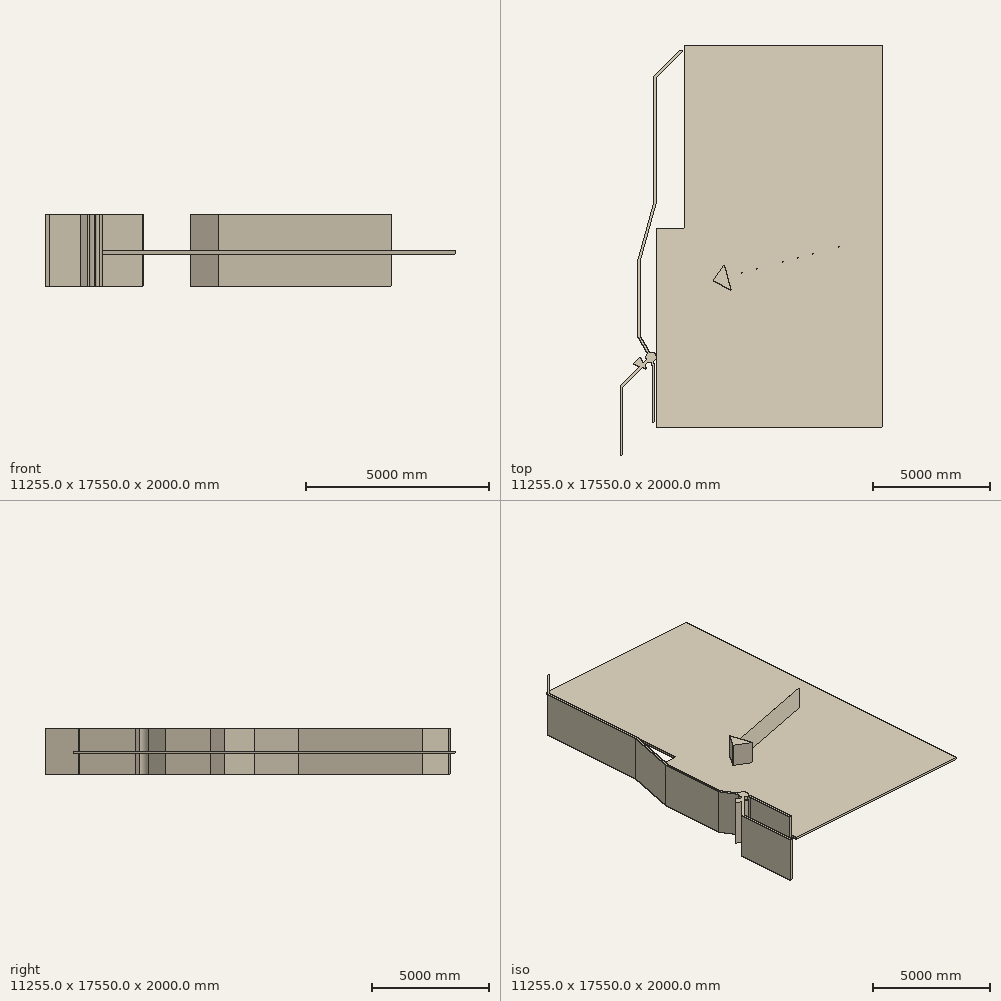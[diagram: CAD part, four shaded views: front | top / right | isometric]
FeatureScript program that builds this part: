
annotation { "Feature Type Name" : "Feature", "Feature Type Description" : "" }
export const myFeature = defineFeature(function(context is Context, id is Id, definition is map)
    precondition{}
    {
        {
            var Q0;
            Q0=qCreatedBy(makeId("Top.planeOp"),FACE);
            var sketch = newSketch(context, id + "F0", { "sketchPlane" : qUnion([Q0])});
            skLineSegment(sketch, "E0", {"start": v(-843.99, -7586.2) * mm, "end": v(-843.99, 913.8) * mm});
            skLineSegment(sketch, "E1", {"start": v(-843.99, 913.8) * mm, "end": v(356.01, 913.8) * mm});
            skLineSegment(sketch, "E2", {"start": v(356.01, 913.8) * mm, "end": v(356.01, 8763.8) * mm});
            skLineSegment(sketch, "E3", {"start": v(-843.99, -7586.2) * mm, "end": v(8856.01, -7586.2) * mm});
            skLineSegment(sketch, "E4", {"start": v(356.01, 8763.8) * mm, "end": v(8856.01, 8763.8) * mm});
            skLineSegment(sketch, "E5", {"start": v(8856.01, 8763.8) * mm, "end": v(8856.01, -7586.2) * mm});
            skSolve(sketch);
        }
        {
            var Q0;
            Q0 = qSketchRegion(id + "F0", true);
            var Q1;
            Q1 = qSketchRegion(id + "F2", true);
            extrude(context, id + "F1", {"entities" : qUnion([Q0, Q1]), "oppositeDirection" : true, "depth" : 100 * mm, "offsetDistance" : 25 * mm});
        }
        {
            var Q0;
            Q0=qCreatedBy(makeId("Top.planeOp"),FACE);
            var sketch = newSketch(context, id + "F2", { "sketchPlane" : qUnion([Q0])});
            skLineSegment(sketch, "E6", {"start": v(231.01, 10518.75) * mm, "end": v(231.01, 5123.53) * mm, "construction": true});
            skLineSegment(sketch, "E7", {"start": v(-3450.5, 8513.8) * mm, "end": v(2709.72, 8513.8) * mm, "construction": true});
            skCircle(sketch, "E8", {"center": v(231.01, 8513.8) * mm, "radius": 55 * mm});
            skLineSegment(sketch, "E9", {"start": v(-893.99, 8769.03) * mm, "end": v(-893.99, 6313.48) * mm, "construction": true});
            skLineSegment(sketch, "E10.bottom", {"start": v(192.12, 8552.7) * mm, "end": v(269.9, 8474.91) * mm});
            skLineSegment(sketch, "E10.left", {"start": v(192.12, 8552.7) * mm, "end": v(-948.99, 7411.58) * mm});
            skLineSegment(sketch, "E10.right", {"start": v(269.9, 8474.91) * mm, "end": v(-838.99, 7366.02) * mm});
            skLineSegment(sketch, "E11.left", {"start": v(-948.99, 7411.58) * mm, "end": v(-948.99, 2043.63) * mm});
            skLineSegment(sketch, "E11.right", {"start": v(-838.99, 7366.02) * mm, "end": v(-838.99, 2028.66) * mm});
            skPoint(sketch, "E12", {"position": v(-838.99, 7366.02) * mm});
            skLineSegment(sketch, "E13.left", {"start": v(-948.99, 2043.63) * mm, "end": v(-1648.99, -480.68) * mm});
            skLineSegment(sketch, "E13.right", {"start": v(-838.99, 2028.66) * mm, "end": v(-1538.99, -495.65) * mm});
            skCircle(sketch, "E14", {"center": v(-1068.99, -4586.2) * mm, "radius": 225 * mm});
            skLineSegment(sketch, "E15.left", {"start": v(-1648.99, -3691.6) * mm, "end": v(-1225.7, -4424.75) * mm});
            skLineSegment(sketch, "E15.right", {"start": v(-1538.99, -3662.13) * mm, "end": v(-1130.44, -4369.75) * mm});
            skLineSegment(sketch, "E16.left", {"start": v(-1184.37, -4779.36) * mm, "end": v(-2288.99, -5883.98) * mm});
            skLineSegment(sketch, "E16.right", {"start": v(-1262.15, -4701.58) * mm, "end": v(-2398.99, -5838.42) * mm});
            skLineSegment(sketch, "E17.left", {"start": v(-1648.99, -480.68) * mm, "end": v(-1648.99, -3691.6) * mm});
            skLineSegment(sketch, "E17.right", {"start": v(-1538.99, -495.65) * mm, "end": v(-1538.99, -3662.13) * mm});
            skPoint(sketch, "E18", {"position": v(-1538.99, -495.65) * mm});
            skPoint(sketch, "E19", {"position": v(-1648.99, -480.68) * mm});
            skPoint(sketch, "E20", {"position": v(-1262.15, -4701.58) * mm});
            skPoint(sketch, "E21", {"position": v(-1184.37, -4779.36) * mm});
            skLineSegment(sketch, "E22.top", {"start": v(-2398.99, -8786.2) * mm, "end": v(-2288.99, -8786.2) * mm});
            skLineSegment(sketch, "E22.left", {"start": v(-2398.99, -5838.42) * mm, "end": v(-2398.99, -8786.2) * mm});
            skLineSegment(sketch, "E22.right", {"start": v(-2288.99, -5883.98) * mm, "end": v(-2288.99, -8786.2) * mm});
            skPoint(sketch, "E23", {"position": v(-2288.99, -5883.98) * mm});
            skPoint(sketch, "E24", {"position": v(-2398.99, -5838.42) * mm});
            skLineSegment(sketch, "E25.bottom", {"start": v(7111.36, 175.71) * mm, "end": v(1591.41, -1303.35) * mm});
            skLineSegment(sketch, "E25.top", {"start": v(7111.87, 173.78) * mm, "end": v(1591.93, -1305.29) * mm});
            skLineSegment(sketch, "E25.left", {"start": v(7111.36, 175.71) * mm, "end": v(7111.87, 173.78) * mm});
            skLineSegment(sketch, "E25.right", {"start": v(1591.41, -1303.35) * mm, "end": v(1591.93, -1305.29) * mm});
            skLineSegment(sketch, "E26", {"start": v(1591.41, -1303.35) * mm, "end": v(2066.27, -623) * mm});
            skLineSegment(sketch, "E27", {"start": v(2066.27, -623) * mm, "end": v(2362.44, -1728.32) * mm});
            skLineSegment(sketch, "E28", {"start": v(2362.44, -1728.32) * mm, "end": v(1591.93, -1305.29) * mm});
            skLineSegment(sketch, "E29", {"start": v(-1527.33, -4581.31) * mm, "end": v(-1241.6, -5102.35) * mm});
            skLineSegment(sketch, "E30", {"start": v(-1241.6, -5102.35) * mm, "end": v(-1829.87, -4883.85) * mm});
            skLineSegment(sketch, "E31", {"start": v(-1829.87, -4883.85) * mm, "end": v(-1527.33, -4581.31) * mm});
            skCircle(sketch, "E32", {"center": v(-968.99, -7336.2) * mm, "radius": 55 * mm});
            skLineSegment(sketch, "E33.left", {"start": v(-959.4, -4782.7) * mm, "end": v(-913.99, -4952.16) * mm});
            skLineSegment(sketch, "E33.right", {"start": v(-1065.64, -4811.17) * mm, "end": v(-1023.99, -4966.64) * mm});
            skPoint(sketch, "E34", {"position": v(-913.99, -4952.16) * mm});
            skPoint(sketch, "E35", {"position": v(-1023.99, -4966.64) * mm});
            skLineSegment(sketch, "E36.trimOffspring", {"start": v(-913.99, -4952.16) * mm, "end": v(-913.99, -7336.2) * mm});
            skLineSegment(sketch, "E37.trimOffspring", {"start": v(-1023.99, -4966.64) * mm, "end": v(-1023.99, -7336.2) * mm});
            skSolve(sketch);
        }
        {
            var Q0;
            Q0 = qSketchRegion(id + "F2", true);
            extrude(context, id + "F3", {"entities" : qUnion([Q0]), "oppositeDirection" : true, "depth" : 1000 * mm, "offsetDistance" : 25 * mm, "hasSecondDirection" : true, "secondDirectionOppositeDirection" : false, "secondDirectionDepth" : 1000 * mm});
        }
    });
